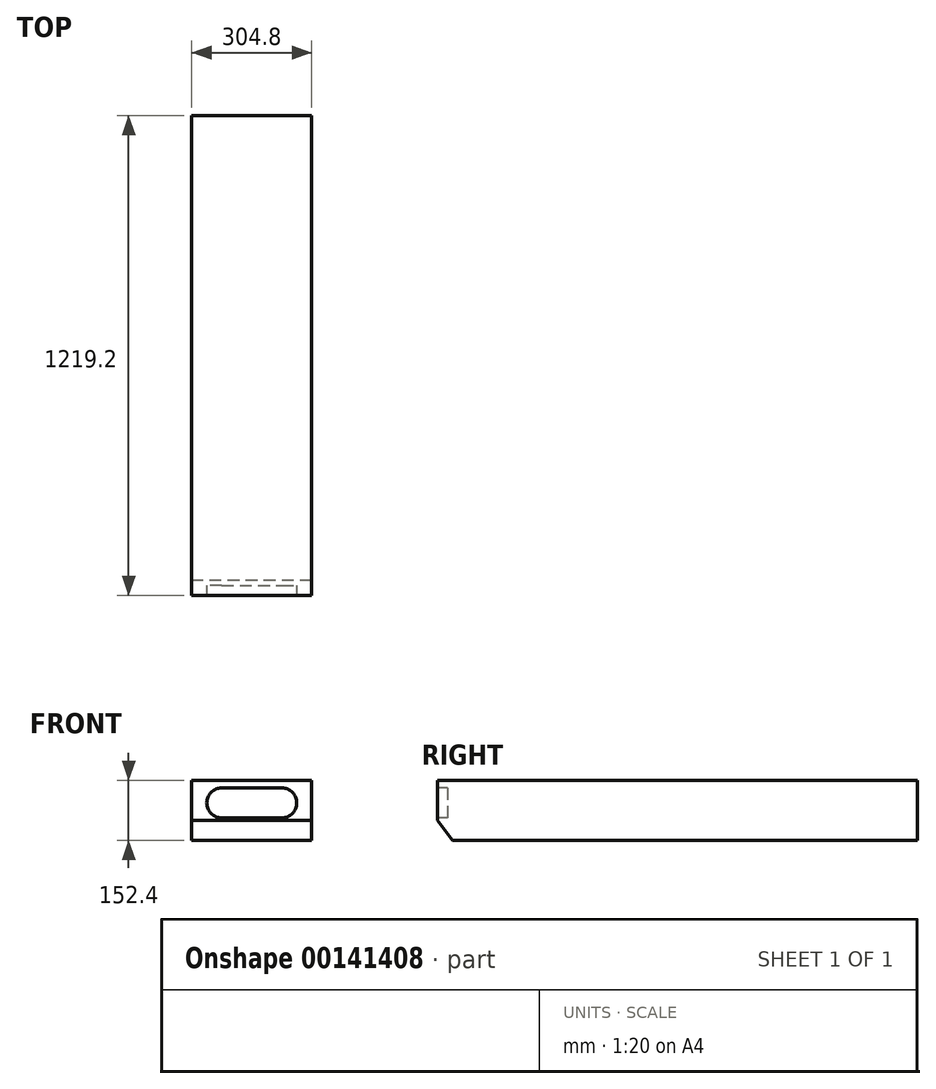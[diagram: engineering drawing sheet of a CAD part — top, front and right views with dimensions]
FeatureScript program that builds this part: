
annotation { "Feature Type Name" : "Feature", "Feature Type Description" : "" }
export const myFeature = defineFeature(function(context is Context, id is Id, definition is map)
    precondition{}
    {
        {
            var Q0;
            Q0=qCreatedBy(makeId("Right.planeOp"),FACE);
            var sketch = newSketch(context, id + "F0", { "sketchPlane" : qUnion([Q0])});
            skLineSegment(sketch, "E0", {"start": v(-609.6, 0) * mm, "end": v(609.6, 0) * mm});
            skLineSegment(sketch, "E1", {"start": v(609.6, 0) * mm, "end": v(609.6, -152.4) * mm});
            skLineSegment(sketch, "E2", {"start": v(609.6, -152.4) * mm, "end": v(-571.5, -152.4) * mm});
            skLineSegment(sketch, "E3", {"start": v(-571.5, -152.4) * mm, "end": v(-609.6, -101.6) * mm});
            skLineSegment(sketch, "E4", {"start": v(-609.6, -101.6) * mm, "end": v(-609.6, 0) * mm});
            skSolve(sketch);
        }
        {
            var Q0;
            Q0 = qSketchRegion(id + "F0", true);
            extrude(context, id + "F1", {"entities" : qUnion([Q0]), "depth" : 304.8 * mm});
        }
        {
            var Q0;
            Q0=makeQuery(id+"F1.opExtrude","SWEPT_FACE",FACE,{"disambiguationData":[OSD([sQuery(id+"F0.wireOp",EDGE,"E4")])]});
            var sketch = newSketch(context, id + "F2", { "sketchPlane" : qUnion([Q0])});
            skLineSegment(sketch, "E5", {"start": v(76.2, -19.05) * mm, "end": v(228.6, -19.05) * mm});
            skLineSegment(sketch, "E6", {"start": v(76.2, -95.25) * mm, "end": v(228.6, -95.25) * mm});
            skArc(sketch, "E7", {"start": v(76.2, -19.05) * mm, "mid": v(38.1, -57.15) * mm, "end": v(76.2, -95.25) * mm});
            skArc(sketch, "E8", {"start": v(228.6, -95.25) * mm, "mid": v(266.7, -57.15) * mm, "end": v(228.6, -19.05) * mm});
            skLineSegment(sketch, "E9", {"start": v(152.4, 0) * mm, "end": v(152.4, -101.6) * mm});
            skSolve(sketch);
        }
        {
            var Q0;
            Q0 = qSketchRegion(id + "F2", true);
            extrude(context, id + "F3", {"entities" : qUnion([Q0]), "operationType" : NewBodyOperationType.REMOVE, "oppositeDirection" : true, "depth" : 25.4 * mm});
        }
    });
